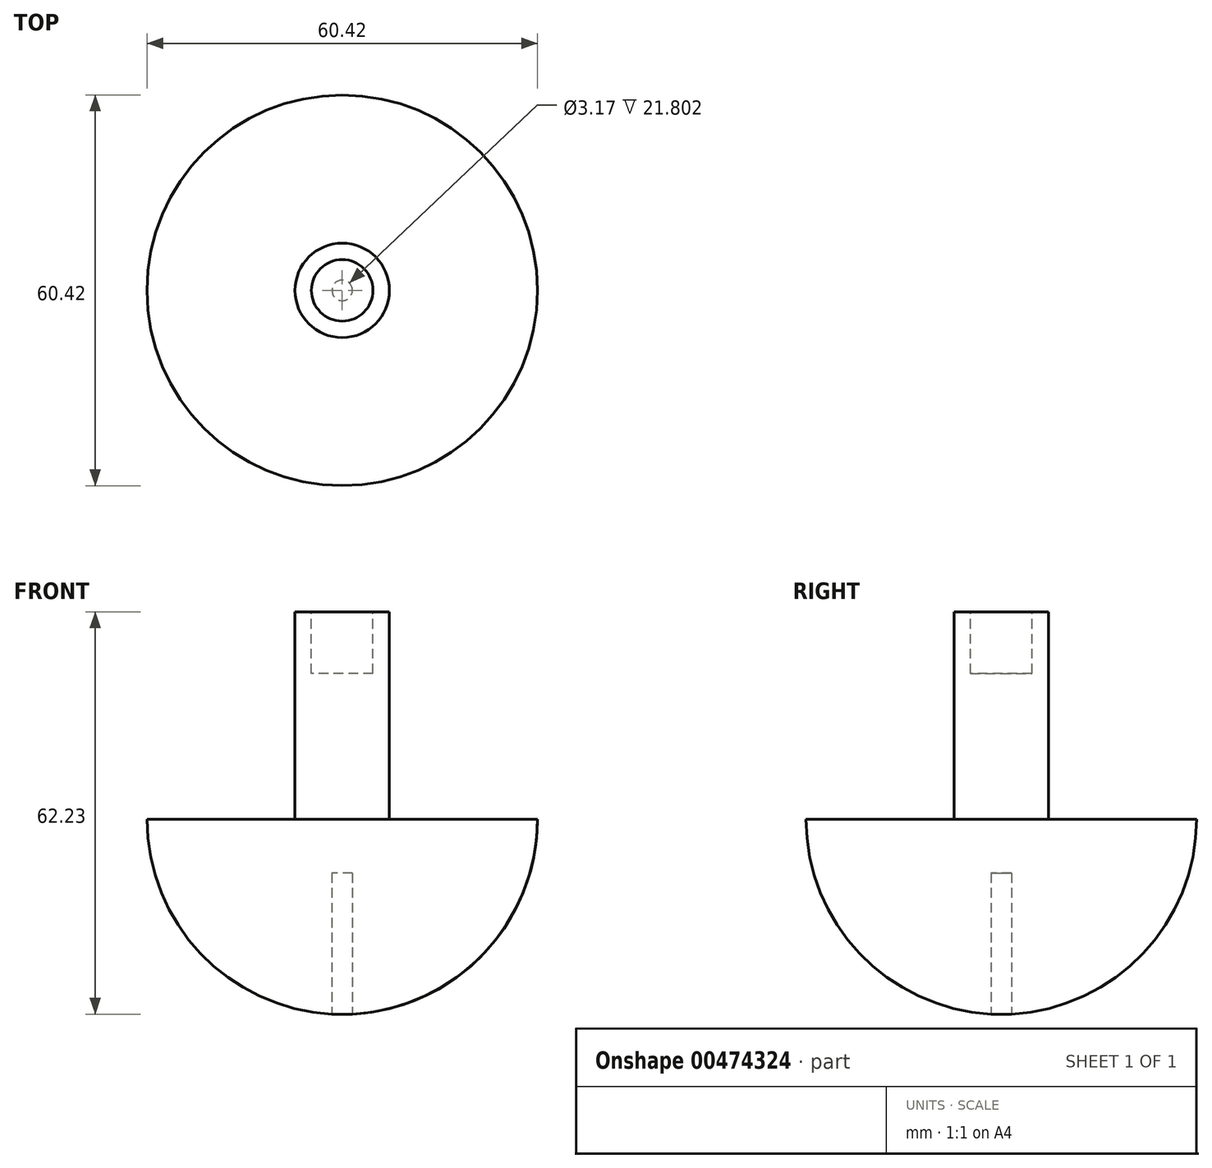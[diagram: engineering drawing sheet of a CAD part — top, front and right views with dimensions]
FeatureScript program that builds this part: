
annotation { "Feature Type Name" : "Feature", "Feature Type Description" : "" }
export const myFeature = defineFeature(function(context is Context, id is Id, definition is map)
    precondition{}
    {
        {
            var Q0;
            Q0=qCreatedBy(makeId("Front.planeOp"),FACE);
            var sketch = newSketch(context, id + "F0", { "sketchPlane" : qUnion([Q0])});
            skArc(sketch, "E0", {"start": v(0, 0) * mm, "mid": v(21.36, 8.85) * mm, "end": v(30.2, 30.2) * mm});
            skLineSegment(sketch, "E1", {"start": v(30.2, 30.2) * mm, "end": v(7.3, 30.2) * mm});
            skLineSegment(sketch, "E2", {"start": v(7.3, 30.2) * mm, "end": v(7.3, 62.27) * mm});
            skLineSegment(sketch, "E3", {"start": v(7.3, 62.27) * mm, "end": v(0, 62.27) * mm});
            skLineSegment(sketch, "E4", {"start": v(0, 62.27) * mm, "end": v(0, 0) * mm});
            skSolve(sketch);
        }
        {
            var Q0;
            Q0=makeQuery(id+"F0.imprint","IMPRINT",FACE,{"disambiguationData":[TD([[makeQuery(id+"F0.imprint","IMPRINT",EDGE,{"derivedFrom":sQuery(id+"F0.wireOp",EDGE,"E0")}),1.0]])]});
            var Q1;
            Q1=sQuery(id+"F0.wireOp",EDGE,"E4");
            revolve(context, id + "F1", {"entities" : qUnion([Q0]), "axis" : qUnion([Q1]), "revolveType" : RevolveType.FULL});
        }
        {
            var Q0;
            Q0=makeQuery(id+"F1.opRevolve","SWEPT_FACE",FACE,{"disambiguationData":[OSD([sQuery(id+"F0.wireOp",EDGE,"E3")])]});
            var sketch = newSketch(context, id + "F2", { "sketchPlane" : qUnion([Q0])});
            skCircle(sketch, "E5", {"center": v(0, 0) * mm, "radius": 4.76 * mm});
            skSolve(sketch);
        }
        {
            var Q0;
            Q0=makeQuery(id+"F2.imprint","IMPRINT",FACE,{"disambiguationData":[TD([[makeQuery(id+"F2.imprint","IMPRINT",EDGE,{"derivedFrom":sQuery(id+"F2.wireOp",EDGE,"E5")}),1.0]])]});
            extrude(context, id + "F3", {"entities" : qUnion([Q0]), "operationType" : NewBodyOperationType.REMOVE, "depth" : -9.52 * mm});
        }
        {
            var Q0;
            Q0=qCreatedBy(makeId("Top.planeOp"),FACE);
            var sketch = newSketch(context, id + "F4", { "sketchPlane" : qUnion([Q0])});
            skCircle(sketch, "E6", {"center": v(0, 0) * mm, "radius": 1.59 * mm});
            skSolve(sketch);
        }
        {
            var Q0;
            Q0=makeQuery(id+"F4.imprint","IMPRINT",FACE,{"disambiguationData":[TD([[makeQuery(id+"F4.imprint","IMPRINT",EDGE,{"derivedFrom":sQuery(id+"F4.wireOp",EDGE,"E6")}),1.0]])]});
            extrude(context, id + "F5", {"entities" : qUnion([Q0]), "operationType" : NewBodyOperationType.REMOVE, "depth" : 21.84 * mm});
        }
    });
